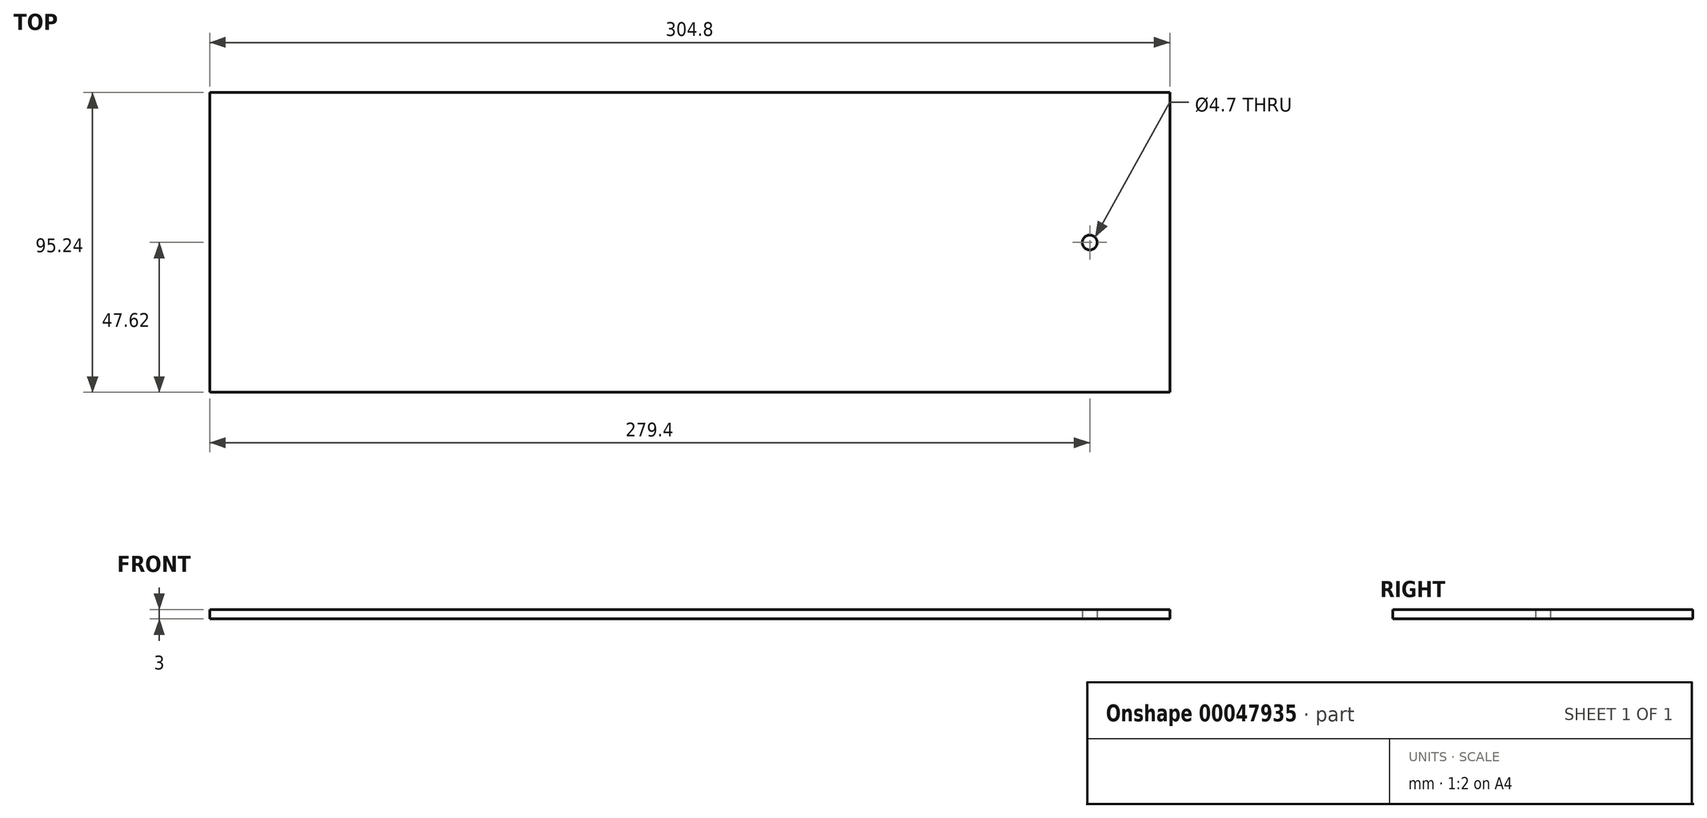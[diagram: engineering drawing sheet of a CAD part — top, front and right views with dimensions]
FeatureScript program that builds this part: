
annotation { "Feature Type Name" : "Feature", "Feature Type Description" : "" }
export const myFeature = defineFeature(function(context is Context, id is Id, definition is map)
    precondition{}
    {
        {
            var Q0;
            Q0=qCreatedBy(makeId("Top.planeOp"),FACE);
            var sketch = newSketch(context, id + "F0", { "sketchPlane" : qUnion([Q0])});
            skLineSegment(sketch, "E0.rect.bottom", {"start": v(-152.4, -47.63) * mm, "end": v(152.4, -47.63) * mm});
            skLineSegment(sketch, "E0.rect.top", {"start": v(-152.4, 47.63) * mm, "end": v(152.4, 47.63) * mm});
            skLineSegment(sketch, "E0.rect.left", {"start": v(-152.4, -47.63) * mm, "end": v(-152.4, 47.63) * mm});
            skLineSegment(sketch, "E0.rect.right", {"start": v(152.4, -47.63) * mm, "end": v(152.4, 47.63) * mm});
            skPoint(sketch, "E0.rect.middle", {"position": v(0, 0) * mm});
            skLineSegment(sketch, "E1.bottom", {"start": v(152.4, -47.63) * mm, "end": v(127, -47.63) * mm, "construction": true});
            skLineSegment(sketch, "E1.top", {"start": v(152.4, 0) * mm, "end": v(127, 0) * mm, "construction": true});
            skLineSegment(sketch, "E1.left", {"start": v(152.4, -47.63) * mm, "end": v(152.4, 0) * mm, "construction": true});
            skLineSegment(sketch, "E1.right", {"start": v(127, -47.63) * mm, "end": v(127, 0) * mm, "construction": true});
            skCircle(sketch, "E2", {"center": v(127, 0) * mm, "radius": 2.35 * mm});
            skSolve(sketch);
        }
        {
            var Q0;
            Q0=makeQuery(id+"F0.imprint","IMPRINT",FACE,{"disambiguationData":[TD([[makeQuery(id+"F0.imprint","IMPRINT",EDGE,{"derivedFrom":sQuery(id+"F0.wireOp",EDGE,"E0.rect.bottom")}),1.0]])]});
            extrude(context, id + "F1", {"entities" : qUnion([Q0]), "depth" : 3 * mm});
        }
    });
